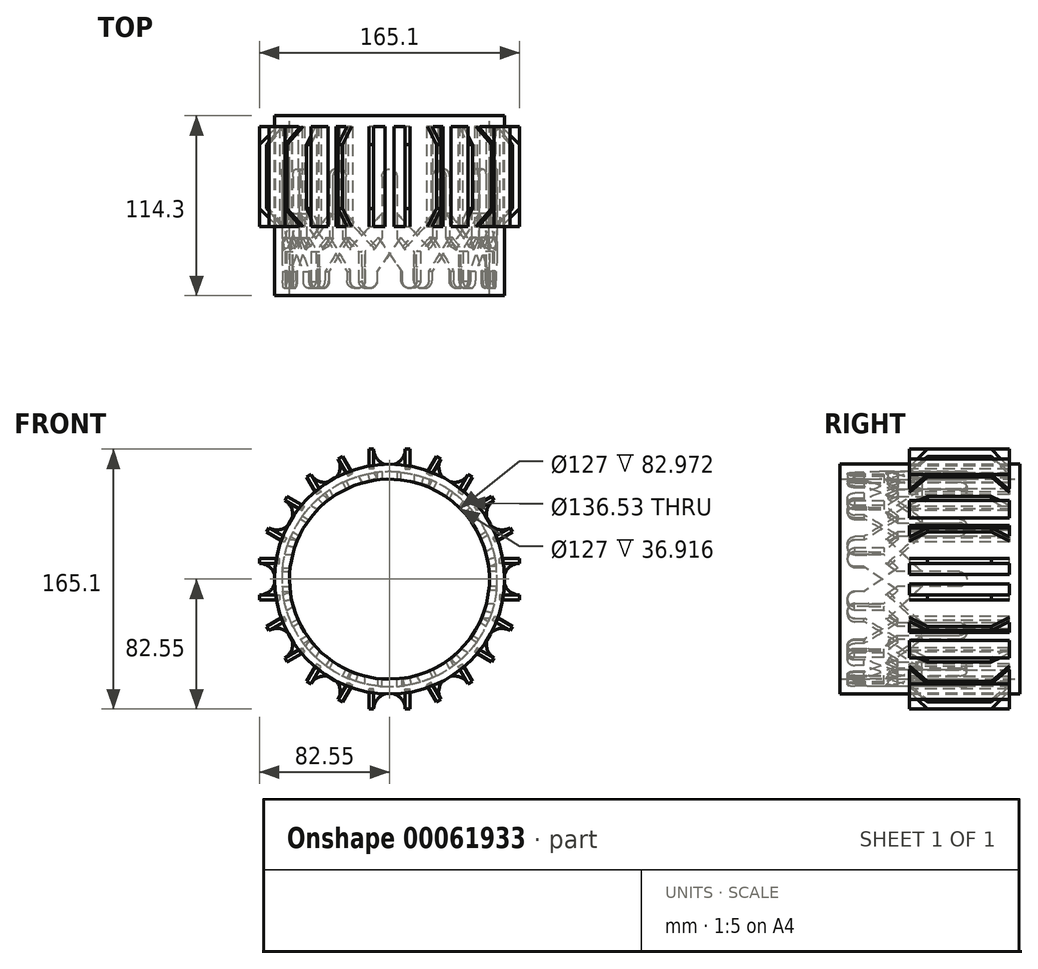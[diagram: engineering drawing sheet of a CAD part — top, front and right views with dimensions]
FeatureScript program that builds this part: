
annotation { "Feature Type Name" : "Feature", "Feature Type Description" : "" }
export const myFeature = defineFeature(function(context is Context, id is Id, definition is map)
    precondition{}
    {
        {
            var Q0;
            Q0=qCreatedBy(makeId("Front.planeOp"),FACE);
            var sketch = newSketch(context, id + "F0", { "sketchPlane" : qUnion([Q0])});
            skCircle(sketch, "E0", {"center": v(0, 0) * mm, "radius": 63.5 * mm});
            skCircle(sketch, "E1.0", {"center": v(0, 0) * mm, "radius": 73.03 * mm});
            skSolve(sketch);
        }
        {
            var Q0;
            Q0=makeQuery(id+"F0.imprint","IMPRINT",FACE,{"disambiguationData":[TD([[makeQuery(id+"F0.imprint","IMPRINT",EDGE,{"derivedFrom":sQuery(id+"F0.wireOp",EDGE,"E0")}),-1.0]])]});
            extrude(context, id + "F1", {"entities" : qUnion([Q0]), "depth" : 114.3 * mm});
        }
        {
            var Q0;
            Q0=qCreatedBy(makeId("Top.planeOp"),FACE);
            cPlane(context, id + "F2", {"entities" : qUnion([Q0]), "cplaneType" : CPlaneType.OFFSET, "offset" : 57.15 * mm, "width" : 152.4 * mm, "height" : 152.4 * mm});
        }
        {
            var Q0;
            Q0=qCreatedBy(id+"F2.planeOp",FACE);
            var sketch = newSketch(context, id + "F3", { "sketchPlane" : qUnion([Q0])});
            skLineSegment(sketch, "E2", {"start": v(0, -38.52) * mm, "end": v(0, -63.92) * mm});
            skCircle(sketch, "E3", {"center": v(20.32, -104.68) * mm, "radius": 4.76 * mm});
            skLineSegment(sketch, "E4.0", {"start": v(4.76, -62.17) * mm, "end": v(25.08, -83.88) * mm});
            skLineSegment(sketch, "E5", {"start": v(25.08, -83.88) * mm, "end": v(25.08, -104.8) * mm});
            skLineSegment(sketch, "E6", {"start": v(4.76, -62.17) * mm, "end": v(4.76, -38.52) * mm});
            skLineSegment(sketch, "E7", {"start": v(-4.76, -77.82) * mm, "end": v(-4.76, -38.52) * mm});
            skCircle(sketch, "E8", {"center": v(0, -38.52) * mm, "radius": 4.76 * mm});
            skLineSegment(sketch, "E9", {"start": v(4.76, -62.17) * mm, "end": v(4.76, -80.82) * mm});
            skLineSegment(sketch, "E10", {"start": v(7.16, -77.38) * mm, "end": v(-7.94, -99) * mm});
            skLineSegment(sketch, "E11", {"start": v(-7.94, -99) * mm, "end": v(-7.94, -104.68) * mm});
            skLineSegment(sketch, "E12.0", {"start": v(-17.46, -96) * mm, "end": v(-17.46, -104.68) * mm});
            skCircle(sketch, "E13", {"center": v(-12.7, -104.68) * mm, "radius": 4.76 * mm});
            skLineSegment(sketch, "E14.0", {"start": v(-4.76, -77.82) * mm, "end": v(-17.46, -96) * mm});
            skLineSegment(sketch, "E15.trimOffspring", {"start": v(7.16, -77.38) * mm, "end": v(15.59, -86.38) * mm});
            skPoint(sketch, "E16.orphan", {"position": v(-4.76, -65.66) * mm});
            skLineSegment(sketch, "E17.0", {"start": v(73.03, -114.3) * mm, "end": v(-73.03, -114.3) * mm});
            skLineSegment(sketch, "E18", {"start": v(15.59, -105.19) * mm, "end": v(15.59, -86.38) * mm});
            skSolve(sketch);
        }
        {
            var Q0;
            {var subQ7=sQuery(id+"F3.wireOp",EDGE,"E6");Q0=makeQuery(id+"F3.imprint","IMPRINT",FACE,{"disambiguationData":[TD([[makeQuery(id+"F3.imprint","IMPRINT",EDGE,{"derivedFrom":subQ7}),1.0]])]});}
            var Q1;
            {var subQ0=sQuery(id+"F3.wireOp",EDGE,"E13");var subQ1=makeQuery(id+"F3.imprint","INTERSECT",VERTEX,{"derivedFrom":[sQuery(id+"F3.wireOp",EDGE,"E11"),subQ0]});Q1=makeQuery(id+"F3.imprint","IMPRINT",FACE,{"disambiguationData":[TD([[makeQuery(id+"F3.imprint","IMPRINT",EDGE,{"disambiguationData":[TD([[subQ1,-1.0]])],"derivedFrom":subQ0}),1.0]])]});}
            var Q2;
            {var subQ0=sQuery(id+"F3.wireOp",EDGE,"E8");var subQ3=makeQuery(id+"F3.imprint","IMPRINT",VERTEX,{"derivedFrom":subQ0});Q2=makeQuery(id+"F3.imprint","IMPRINT",FACE,{"disambiguationData":[TD([[makeQuery(id+"F3.imprint","IMPRINT",EDGE,{"disambiguationData":[TD([[subQ3,1.0]])],"derivedFrom":subQ0}),1.0]])]});}
            var Q3;
            {var subQ1=sQuery(id+"F3.wireOp",EDGE,"E4.0");Q3=makeQuery(id+"F3.imprint","IMPRINT",FACE,{"disambiguationData":[TD([[makeQuery(id+"F3.imprint","IMPRINT",EDGE,{"derivedFrom":subQ1}),-1.0]])]});}
            var Q4;
            {var subQ0=sQuery(id+"F3.wireOp",EDGE,"E3");var subQ1=makeQuery(id+"F3.imprint","INTERSECT",VERTEX,{"derivedFrom":[subQ0,sQuery(id+"F3.wireOp",EDGE,"55f282a2-0efb-42c4-87fe-9c5e402fcb43.0")]});Q4=makeQuery(id+"F3.imprint","IMPRINT",FACE,{"disambiguationData":[TD([[makeQuery(id+"F3.imprint","IMPRINT",EDGE,{"disambiguationData":[TD([[subQ1,1.0]])],"derivedFrom":subQ0}),1.0]])]});}
            extrude(context, id + "F4", {"entities" : qUnion([Q0, Q1, Q2, Q3, Q4]), "depth" : 19.05 * mm});
        }
        {
            var Q0;
            Q0=makeQuery(id+"F4.opExtrude","SWEPT_BODY",BODY,{"disambiguationData":[OSD([sQuery(id+"F3.wireOp",EDGE,"E3"),sQuery(id+"F3.wireOp",EDGE,"E4.0"),sQuery(id+"F3.wireOp",EDGE,"E5"),sQuery(id+"F3.wireOp",EDGE,"E6"),sQuery(id+"F3.wireOp",EDGE,"E7"),sQuery(id+"F3.wireOp",EDGE,"E8"),sQuery(id+"F3.wireOp",EDGE,"55f282a2-0efb-42c4-87fe-9c5e402fcb43.0"),sQuery(id+"F3.wireOp",EDGE,"E10"),sQuery(id+"F3.wireOp",EDGE,"E11"),sQuery(id+"F3.wireOp",EDGE,"E12.0"),sQuery(id+"F3.wireOp",EDGE,"E13"),sQuery(id+"F3.wireOp",EDGE,"E14.0"),sQuery(id+"F3.wireOp",EDGE,"E15.trimOffspring")])]});
            var Q1;
            Q1=makeQuery(id+"F1.opExtrude","SWEPT_FACE",FACE,{"disambiguationData":[OSD([sQuery(id+"F0.wireOp",EDGE,"E0")])]});
            circularPattern(context, id + "F5", {"entities" : qUnion([Q0]), "axis" : qUnion([Q1]), "angle" : 30 * degree, "instanceCount" : 12});
        }
        {
            var Q0;
            Q0=makeQuery(id+"F5.opPattern","COPY",BODY,{"derivedFrom":makeQuery(id+"F4.opExtrude","SWEPT_BODY",BODY,{"disambiguationData":[OSD([sQuery(id+"F3.wireOp",EDGE,"E3"),sQuery(id+"F3.wireOp",EDGE,"E4.0"),sQuery(id+"F3.wireOp",EDGE,"E5"),sQuery(id+"F3.wireOp",EDGE,"E6"),sQuery(id+"F3.wireOp",EDGE,"E7"),sQuery(id+"F3.wireOp",EDGE,"E8"),sQuery(id+"F3.wireOp",EDGE,"55f282a2-0efb-42c4-87fe-9c5e402fcb43.0"),sQuery(id+"F3.wireOp",EDGE,"E10"),sQuery(id+"F3.wireOp",EDGE,"E11"),sQuery(id+"F3.wireOp",EDGE,"E12.0"),sQuery(id+"F3.wireOp",EDGE,"E13"),sQuery(id+"F3.wireOp",EDGE,"E14.0"),sQuery(id+"F3.wireOp",EDGE,"E15.trimOffspring")])]}),"instanceName":"1"});
            var Q1;
            Q1=makeQuery(id+"F4.opExtrude","SWEPT_BODY",BODY,{"disambiguationData":[OSD([sQuery(id+"F3.wireOp",EDGE,"E3"),sQuery(id+"F3.wireOp",EDGE,"E4.0"),sQuery(id+"F3.wireOp",EDGE,"E5"),sQuery(id+"F3.wireOp",EDGE,"E6"),sQuery(id+"F3.wireOp",EDGE,"E7"),sQuery(id+"F3.wireOp",EDGE,"E8"),sQuery(id+"F3.wireOp",EDGE,"55f282a2-0efb-42c4-87fe-9c5e402fcb43.0"),sQuery(id+"F3.wireOp",EDGE,"E10"),sQuery(id+"F3.wireOp",EDGE,"E11"),sQuery(id+"F3.wireOp",EDGE,"E12.0"),sQuery(id+"F3.wireOp",EDGE,"E13"),sQuery(id+"F3.wireOp",EDGE,"E14.0"),sQuery(id+"F3.wireOp",EDGE,"E15.trimOffspring")])]});
            var Q2;
            Q2=makeQuery(id+"F5.opPattern","COPY",BODY,{"derivedFrom":makeQuery(id+"F4.opExtrude","SWEPT_BODY",BODY,{"disambiguationData":[OSD([sQuery(id+"F3.wireOp",EDGE,"E3"),sQuery(id+"F3.wireOp",EDGE,"E4.0"),sQuery(id+"F3.wireOp",EDGE,"E5"),sQuery(id+"F3.wireOp",EDGE,"E6"),sQuery(id+"F3.wireOp",EDGE,"E7"),sQuery(id+"F3.wireOp",EDGE,"E8"),sQuery(id+"F3.wireOp",EDGE,"55f282a2-0efb-42c4-87fe-9c5e402fcb43.0"),sQuery(id+"F3.wireOp",EDGE,"E10"),sQuery(id+"F3.wireOp",EDGE,"E11"),sQuery(id+"F3.wireOp",EDGE,"E12.0"),sQuery(id+"F3.wireOp",EDGE,"E13"),sQuery(id+"F3.wireOp",EDGE,"E14.0"),sQuery(id+"F3.wireOp",EDGE,"E15.trimOffspring")])]}),"instanceName":"9"});
            var Q3;
            Q3=makeQuery(id+"F5.opPattern","COPY",BODY,{"derivedFrom":makeQuery(id+"F4.opExtrude","SWEPT_BODY",BODY,{"disambiguationData":[OSD([sQuery(id+"F3.wireOp",EDGE,"E3"),sQuery(id+"F3.wireOp",EDGE,"E4.0"),sQuery(id+"F3.wireOp",EDGE,"E5"),sQuery(id+"F3.wireOp",EDGE,"E6"),sQuery(id+"F3.wireOp",EDGE,"E7"),sQuery(id+"F3.wireOp",EDGE,"E8"),sQuery(id+"F3.wireOp",EDGE,"55f282a2-0efb-42c4-87fe-9c5e402fcb43.0"),sQuery(id+"F3.wireOp",EDGE,"E10"),sQuery(id+"F3.wireOp",EDGE,"E11"),sQuery(id+"F3.wireOp",EDGE,"E12.0"),sQuery(id+"F3.wireOp",EDGE,"E13"),sQuery(id+"F3.wireOp",EDGE,"E14.0"),sQuery(id+"F3.wireOp",EDGE,"E15.trimOffspring")])]}),"instanceName":"4"});
            var Q4;
            Q4=makeQuery(id+"F5.opPattern","COPY",BODY,{"derivedFrom":makeQuery(id+"F4.opExtrude","SWEPT_BODY",BODY,{"disambiguationData":[OSD([sQuery(id+"F3.wireOp",EDGE,"E3"),sQuery(id+"F3.wireOp",EDGE,"E4.0"),sQuery(id+"F3.wireOp",EDGE,"E5"),sQuery(id+"F3.wireOp",EDGE,"E6"),sQuery(id+"F3.wireOp",EDGE,"E7"),sQuery(id+"F3.wireOp",EDGE,"E8"),sQuery(id+"F3.wireOp",EDGE,"55f282a2-0efb-42c4-87fe-9c5e402fcb43.0"),sQuery(id+"F3.wireOp",EDGE,"E10"),sQuery(id+"F3.wireOp",EDGE,"E11"),sQuery(id+"F3.wireOp",EDGE,"E12.0"),sQuery(id+"F3.wireOp",EDGE,"E13"),sQuery(id+"F3.wireOp",EDGE,"E14.0"),sQuery(id+"F3.wireOp",EDGE,"E15.trimOffspring")])]}),"instanceName":"3"});
            var Q5;
            Q5=makeQuery(id+"F5.opPattern","COPY",BODY,{"derivedFrom":makeQuery(id+"F4.opExtrude","SWEPT_BODY",BODY,{"disambiguationData":[OSD([sQuery(id+"F3.wireOp",EDGE,"E3"),sQuery(id+"F3.wireOp",EDGE,"E4.0"),sQuery(id+"F3.wireOp",EDGE,"E5"),sQuery(id+"F3.wireOp",EDGE,"E6"),sQuery(id+"F3.wireOp",EDGE,"E7"),sQuery(id+"F3.wireOp",EDGE,"E8"),sQuery(id+"F3.wireOp",EDGE,"55f282a2-0efb-42c4-87fe-9c5e402fcb43.0"),sQuery(id+"F3.wireOp",EDGE,"E10"),sQuery(id+"F3.wireOp",EDGE,"E11"),sQuery(id+"F3.wireOp",EDGE,"E12.0"),sQuery(id+"F3.wireOp",EDGE,"E13"),sQuery(id+"F3.wireOp",EDGE,"E14.0"),sQuery(id+"F3.wireOp",EDGE,"E15.trimOffspring")])]}),"instanceName":"5"});
            var Q6;
            Q6=makeQuery(id+"F5.opPattern","COPY",BODY,{"derivedFrom":makeQuery(id+"F4.opExtrude","SWEPT_BODY",BODY,{"disambiguationData":[OSD([sQuery(id+"F3.wireOp",EDGE,"E3"),sQuery(id+"F3.wireOp",EDGE,"E4.0"),sQuery(id+"F3.wireOp",EDGE,"E5"),sQuery(id+"F3.wireOp",EDGE,"E6"),sQuery(id+"F3.wireOp",EDGE,"E7"),sQuery(id+"F3.wireOp",EDGE,"E8"),sQuery(id+"F3.wireOp",EDGE,"55f282a2-0efb-42c4-87fe-9c5e402fcb43.0"),sQuery(id+"F3.wireOp",EDGE,"E10"),sQuery(id+"F3.wireOp",EDGE,"E11"),sQuery(id+"F3.wireOp",EDGE,"E12.0"),sQuery(id+"F3.wireOp",EDGE,"E13"),sQuery(id+"F3.wireOp",EDGE,"E14.0"),sQuery(id+"F3.wireOp",EDGE,"E15.trimOffspring")])]}),"instanceName":"6"});
            var Q7;
            Q7=makeQuery(id+"F5.opPattern","COPY",BODY,{"derivedFrom":makeQuery(id+"F4.opExtrude","SWEPT_BODY",BODY,{"disambiguationData":[OSD([sQuery(id+"F3.wireOp",EDGE,"E3"),sQuery(id+"F3.wireOp",EDGE,"E4.0"),sQuery(id+"F3.wireOp",EDGE,"E5"),sQuery(id+"F3.wireOp",EDGE,"E6"),sQuery(id+"F3.wireOp",EDGE,"E7"),sQuery(id+"F3.wireOp",EDGE,"E8"),sQuery(id+"F3.wireOp",EDGE,"55f282a2-0efb-42c4-87fe-9c5e402fcb43.0"),sQuery(id+"F3.wireOp",EDGE,"E10"),sQuery(id+"F3.wireOp",EDGE,"E11"),sQuery(id+"F3.wireOp",EDGE,"E12.0"),sQuery(id+"F3.wireOp",EDGE,"E13"),sQuery(id+"F3.wireOp",EDGE,"E14.0"),sQuery(id+"F3.wireOp",EDGE,"E15.trimOffspring")])]}),"instanceName":"7"});
            var Q8;
            Q8=makeQuery(id+"F5.opPattern","COPY",BODY,{"derivedFrom":makeQuery(id+"F4.opExtrude","SWEPT_BODY",BODY,{"disambiguationData":[OSD([sQuery(id+"F3.wireOp",EDGE,"E3"),sQuery(id+"F3.wireOp",EDGE,"E4.0"),sQuery(id+"F3.wireOp",EDGE,"E5"),sQuery(id+"F3.wireOp",EDGE,"E6"),sQuery(id+"F3.wireOp",EDGE,"E7"),sQuery(id+"F3.wireOp",EDGE,"E8"),sQuery(id+"F3.wireOp",EDGE,"55f282a2-0efb-42c4-87fe-9c5e402fcb43.0"),sQuery(id+"F3.wireOp",EDGE,"E10"),sQuery(id+"F3.wireOp",EDGE,"E11"),sQuery(id+"F3.wireOp",EDGE,"E12.0"),sQuery(id+"F3.wireOp",EDGE,"E13"),sQuery(id+"F3.wireOp",EDGE,"E14.0"),sQuery(id+"F3.wireOp",EDGE,"E15.trimOffspring")])]}),"instanceName":"8"});
            var Q9;
            Q9=makeQuery(id+"F5.opPattern","COPY",BODY,{"derivedFrom":makeQuery(id+"F4.opExtrude","SWEPT_BODY",BODY,{"disambiguationData":[OSD([sQuery(id+"F3.wireOp",EDGE,"E3"),sQuery(id+"F3.wireOp",EDGE,"E4.0"),sQuery(id+"F3.wireOp",EDGE,"E5"),sQuery(id+"F3.wireOp",EDGE,"E6"),sQuery(id+"F3.wireOp",EDGE,"E7"),sQuery(id+"F3.wireOp",EDGE,"E8"),sQuery(id+"F3.wireOp",EDGE,"55f282a2-0efb-42c4-87fe-9c5e402fcb43.0"),sQuery(id+"F3.wireOp",EDGE,"E10"),sQuery(id+"F3.wireOp",EDGE,"E11"),sQuery(id+"F3.wireOp",EDGE,"E12.0"),sQuery(id+"F3.wireOp",EDGE,"E13"),sQuery(id+"F3.wireOp",EDGE,"E14.0"),sQuery(id+"F3.wireOp",EDGE,"E15.trimOffspring")])]}),"instanceName":"10"});
            var Q10;
            Q10=makeQuery(id+"F5.opPattern","COPY",BODY,{"derivedFrom":makeQuery(id+"F4.opExtrude","SWEPT_BODY",BODY,{"disambiguationData":[OSD([sQuery(id+"F3.wireOp",EDGE,"E3"),sQuery(id+"F3.wireOp",EDGE,"E4.0"),sQuery(id+"F3.wireOp",EDGE,"E5"),sQuery(id+"F3.wireOp",EDGE,"E6"),sQuery(id+"F3.wireOp",EDGE,"E7"),sQuery(id+"F3.wireOp",EDGE,"E8"),sQuery(id+"F3.wireOp",EDGE,"55f282a2-0efb-42c4-87fe-9c5e402fcb43.0"),sQuery(id+"F3.wireOp",EDGE,"E10"),sQuery(id+"F3.wireOp",EDGE,"E11"),sQuery(id+"F3.wireOp",EDGE,"E12.0"),sQuery(id+"F3.wireOp",EDGE,"E13"),sQuery(id+"F3.wireOp",EDGE,"E14.0"),sQuery(id+"F3.wireOp",EDGE,"E15.trimOffspring")])]}),"instanceName":"11"});
            var Q11;
            Q11=makeQuery(id+"F5.opPattern","COPY",BODY,{"derivedFrom":makeQuery(id+"F4.opExtrude","SWEPT_BODY",BODY,{"disambiguationData":[OSD([sQuery(id+"F3.wireOp",EDGE,"E3"),sQuery(id+"F3.wireOp",EDGE,"E4.0"),sQuery(id+"F3.wireOp",EDGE,"E5"),sQuery(id+"F3.wireOp",EDGE,"E6"),sQuery(id+"F3.wireOp",EDGE,"E7"),sQuery(id+"F3.wireOp",EDGE,"E8"),sQuery(id+"F3.wireOp",EDGE,"E10"),sQuery(id+"F3.wireOp",EDGE,"E11"),sQuery(id+"F3.wireOp",EDGE,"E12.0"),sQuery(id+"F3.wireOp",EDGE,"E13"),sQuery(id+"F3.wireOp",EDGE,"E14.0"),sQuery(id+"F3.wireOp",EDGE,"E15.trimOffspring"),sQuery(id+"F3.wireOp",EDGE,"E18")])]}),"instanceName":"2"});
            var Q12;
            Q12=makeQuery(id+"F1.opExtrude","SWEPT_BODY",BODY,{"disambiguationData":[OSD([sQuery(id+"F0.wireOp",EDGE,"E0"),sQuery(id+"F0.wireOp",EDGE,"E1.0")])]});
            booleanBodies(context, id + "F6", {"operationType" : BooleanOperationType.SUBTRACTION, "tools" : qUnion([Q0, Q1, Q2, Q3, Q4, Q5, Q6, Q7, Q8, Q9, Q10, Q11]), "targets" : qUnion([Q12])});
        }
        {
            var Q0;
            Q0=makeQuery(id+"F1.opExtrude","CAP_FACE",FACE,{"disambiguationData":[OSD([sQuery(id+"F0.wireOp",EDGE,"E0"),sQuery(id+"F0.wireOp",EDGE,"E1.0")])],"isStart":false});
            var sketch = newSketch(context, id + "F7", { "sketchPlane" : qUnion([Q0])});
            skCircle(sketch, "E19.0", {"center": v(0, 0) * mm, "radius": 73.03 * mm});
            skCircle(sketch, "E20.0", {"center": v(0, 0) * mm, "radius": 68.26 * mm});
            skSolve(sketch);
        }
        {
            var Q0;
            Q0=makeQuery(id+"F7.imprint","IMPRINT",FACE,{"disambiguationData":[TD([[makeQuery(id+"F7.imprint","IMPRINT",EDGE,{"derivedFrom":sQuery(id+"F7.wireOp",EDGE,"E19.0")}),1.0]])]});
            var Q1;
            Q1=makeQuery(id+"F1.opExtrude","CAP_FACE",FACE,{"disambiguationData":[OSD([sQuery(id+"F0.wireOp",EDGE,"E0"),sQuery(id+"F0.wireOp",EDGE,"E1.0")])],"isStart":true});
            extrude(context, id + "F8", {"entities" : qUnion([Q0]), "endBound" : BoundingType.UP_TO_SURFACE, "oppositeDirection" : true, "endBoundEntityFace" : qUnion([Q1]), "depth" : 25.4 * mm});
        }
        {
            var Q0;
            Q0=makeQuery(id+"F6.opBoolean","SPLIT",BODY,{"disambiguationData":[OD(0.0)],"derivedFrom":makeQuery(id+"F1.opExtrude","SWEPT_BODY",BODY,{"disambiguationData":[OSD([sQuery(id+"F0.wireOp",EDGE,"E0"),sQuery(id+"F0.wireOp",EDGE,"E1.0")])]})});
            var Q1;
            Q1=makeQuery(id+"F6.opBoolean","SPLIT",BODY,{"disambiguationData":[OD(1.0)],"derivedFrom":makeQuery(id+"F1.opExtrude","SWEPT_BODY",BODY,{"disambiguationData":[OSD([sQuery(id+"F0.wireOp",EDGE,"E0"),sQuery(id+"F0.wireOp",EDGE,"E1.0")])]})});
            var Q2;
            Q2=makeQuery(id+"F8.opExtrude","SWEPT_BODY",BODY,{"disambiguationData":[OSD([sQuery(id+"F7.wireOp",EDGE,"E19.0"),sQuery(id+"F7.wireOp",EDGE,"E20.0")])]});
            booleanBodies(context, id + "F9", {"operationType" : BooleanOperationType.UNION, "tools" : qUnion([Q0, Q1, Q2])});
        }
        {
            var Q0;
            Q0=qCreatedBy(id+"F2.planeOp",FACE);
            cPlane(context, id + "F10", {"entities" : qUnion([Q0]), "cplaneType" : CPlaneType.OFFSET, "offset" : 12.7 * mm, "width" : 152.4 * mm, "height" : 152.4 * mm});
        }
        {
            var Q0;
            Q0=qCreatedBy(id+"F10.planeOp",FACE);
            var sketch = newSketch(context, id + "F11", { "sketchPlane" : qUnion([Q0])});
            skLineSegment(sketch, "E21.0", {"start": v(-4.76, -77.82) * mm, "end": v(-4.76, -38.52) * mm});
            skLineSegment(sketch, "E22.0", {"start": v(4.76, -62.17) * mm, "end": v(4.76, -38.52) * mm});
            skLineSegment(sketch, "E23", {"start": v(-4.76, -38.52) * mm, "end": v(4.76, -38.52) * mm});
            skLineSegment(sketch, "E24.rect.left", {"start": v(-10, -6.77) * mm, "end": v(-10, -70.27) * mm});
            skLineSegment(sketch, "E24.rect.right", {"start": v(10, -6.77) * mm, "end": v(10, -70.27) * mm});
            skPoint(sketch, "E24.rect.middle", {"position": v(0, -38.52) * mm});
            skLineSegment(sketch, "E25", {"start": v(-13.13, -6.77) * mm, "end": v(-13.13, -70.27) * mm});
            skLineSegment(sketch, "E26", {"start": v(-10, -6.77) * mm, "end": v(-13.13, -6.77) * mm});
            skLineSegment(sketch, "E27", {"start": v(-13.13, -70.27) * mm, "end": v(-10, -70.27) * mm});
            skSolve(sketch);
        }
        {
            var Q0;
            Q0 = qSketchRegion(id + "F11", true);
            extrude(context, id + "F12", {"entities" : qUnion([Q0]), "depth" : 12.7 * mm});
        }
        {
            var Q0;
            Q0=makeQuery(id+"F12.opExtrude","SWEPT_BODY",BODY,{"disambiguationData":[OSD([sQuery(id+"F11.wireOp",EDGE,"E24.rect.left"),sQuery(id+"F11.wireOp",EDGE,"E25"),sQuery(id+"F11.wireOp",EDGE,"E27"),sQuery(id+"F11.wireOp",EDGE,"E26")])]});
            var Q1;
            Q1=qCreatedBy(makeId("Right.planeOp"),FACE);
            mirror(context, id + "F13", {"entities" : qUnion([Q0]), "mirrorPlane" : qUnion([Q1])});
        }
        {
            var Q0;
            Q0=makeQuery(id+"F13.opPattern","COPY",FACE,{"derivedFrom":makeQuery(id+"F12.opExtrude","SWEPT_FACE",FACE,{"disambiguationData":[OSD([sQuery(id+"F11.wireOp",EDGE,"E26")])]}),"instanceName":"1"});
            var sketch = newSketch(context, id + "F14", { "sketchPlane" : qUnion([Q0])});
            skCircle(sketch, "E28.0", {"center": v(0, 0) * mm, "radius": 73.03 * mm});
            skLineSegment(sketch, "E29.0", {"start": v(10, 82.55) * mm, "end": v(13.13, 82.55) * mm});
            skLineSegment(sketch, "E30.0", {"start": v(-10, 82.55) * mm, "end": v(-13.13, 82.55) * mm});
            skLineSegment(sketch, "E31", {"start": v(10, 82.55) * mm, "end": v(10, 72.34) * mm});
            skPoint(sketch, "E32.endSnap0", {"position": v(-10, 76.2) * mm});
            skPoint(sketch, "E32.endSnap1", {"position": v(10, 77.44) * mm});
            skLineSegment(sketch, "E33", {"start": v(10, 82.55) * mm, "end": v(-10, 82.55) * mm});
            skArc(sketch, "E34", {"start": v(-10, 82.55) * mm, "mid": v(-8.03, 76.58) * mm, "end": v(-2.89, 72.97) * mm});
            skArc(sketch, "E35", {"start": v(10, 82.55) * mm, "mid": v(8.03, 76.58) * mm, "end": v(2.89, 72.97) * mm});
            skPoint(sketch, "E36.orphan", {"position": v(0, 72.54) * mm});
            skSolve(sketch);
        }
        {
            var Q0;
            {var subQ0=sQuery(id+"F14.wireOp",EDGE,"E34");Q0=makeQuery(id+"F14.imprint","IMPRINT",FACE,{"disambiguationData":[TD([[makeQuery(id+"F14.imprint","IMPRINT",EDGE,{"derivedFrom":subQ0}),-1.0]])]});}
            var Q1;
            {var subQ0=sQuery(id+"F14.wireOp",EDGE,"E31");Q1=makeQuery(id+"F14.imprint","IMPRINT",FACE,{"disambiguationData":[TD([[makeQuery(id+"F14.imprint","IMPRINT",EDGE,{"derivedFrom":subQ0}),-1.0]])]});}
            var Q2;
            Q2=makeQuery(id+"F13.opPattern","COPY",FACE,{"derivedFrom":makeQuery(id+"F12.opExtrude","SWEPT_FACE",FACE,{"disambiguationData":[OSD([sQuery(id+"F11.wireOp",EDGE,"E27")])]}),"instanceName":"1"});
            extrude(context, id + "F15", {"entities" : qUnion([Q0, Q1]), "endBound" : BoundingType.UP_TO_SURFACE, "oppositeDirection" : true, "endBoundEntityFace" : qUnion([Q2]), "depth" : 25.4 * mm});
        }
        {
            var Q0;
            Q0=makeQuery(id+"F13.opPattern","COPY",EDGE,{"derivedFrom":makeQuery(id+"F12.opExtrude","CAP_EDGE",EDGE,{"disambiguationData":[OSD([sQuery(id+"F11.wireOp",EDGE,"E26")])],"isStart":false}),"instanceName":"1"});
            var Q1;
            Q1=makeQuery(id+"F12.opExtrude","CAP_EDGE",EDGE,{"disambiguationData":[OSD([sQuery(id+"F11.wireOp",EDGE,"E26")])],"isStart":false});
            var Q2;
            Q2=makeQuery(id+"F12.opExtrude","CAP_EDGE",EDGE,{"disambiguationData":[OSD([sQuery(id+"F11.wireOp",EDGE,"E27")])],"isStart":false});
            var Q3;
            Q3=makeQuery(id+"F13.opPattern","COPY",EDGE,{"derivedFrom":makeQuery(id+"F12.opExtrude","CAP_EDGE",EDGE,{"disambiguationData":[OSD([sQuery(id+"F11.wireOp",EDGE,"E27")])],"isStart":false}),"instanceName":"1"});
            chamfer(context, id + "F16", {"entities" : qUnion([Q0, Q1, Q2, Q3]), "width" : 11.43 * mm, "tangentPropagation" : true});
        }
        {
            var Q0;
            Q0=makeQuery(id+"F13.opPattern","COPY",BODY,{"derivedFrom":makeQuery(id+"F12.opExtrude","SWEPT_BODY",BODY,{"disambiguationData":[OSD([sQuery(id+"F11.wireOp",EDGE,"E24.rect.left"),sQuery(id+"F11.wireOp",EDGE,"E25"),sQuery(id+"F11.wireOp",EDGE,"E27"),sQuery(id+"F11.wireOp",EDGE,"E26")])]}),"instanceName":"1"});
            var Q1;
            Q1=makeQuery(id+"F12.opExtrude","SWEPT_BODY",BODY,{"disambiguationData":[OSD([sQuery(id+"F11.wireOp",EDGE,"E24.rect.left"),sQuery(id+"F11.wireOp",EDGE,"E25"),sQuery(id+"F11.wireOp",EDGE,"E27"),sQuery(id+"F11.wireOp",EDGE,"E26")])]});
            var Q2;
            Q2=makeQuery(id+"F15.opExtrude","SWEPT_BODY",BODY,{"disambiguationData":[OSD([sQuery(id+"F14.wireOp",EDGE,"E28.0"),sQuery(id+"F14.wireOp",EDGE,"E31"),sQuery(id+"F14.wireOp",EDGE,"E35")])]});
            var Q3;
            Q3=makeQuery(id+"F15.opExtrude","SWEPT_BODY",BODY,{"disambiguationData":[OSD([sQuery(id+"F11.wireOp",EDGE,"E24.rect.left"),sQuery(id+"F11.wireOp",EDGE,"E26"),sQuery(id+"F14.wireOp",EDGE,"E28.0"),sQuery(id+"F14.wireOp",EDGE,"E34")])]});
            var Q4;
            {var subQ0=makeQuery(id+"F4.opExtrude","SWEPT_FACE",FACE,{"disambiguationData":[OSD([sQuery(id+"F3.wireOp",EDGE,"E3")])]});var subQ6=sQuery(id+"F0.wireOp",EDGE,"E1.0");var subQ8=makeQuery(id+"F1.opExtrude","SWEPT_FACE",FACE,{"disambiguationData":[OSD([subQ6])]});var subQ9=makeQuery(id+"F4.opExtrude","SWEPT_FACE",FACE,{"disambiguationData":[OSD([sQuery(id+"F3.wireOp",EDGE,"E4.0")])]});Q4=makeQuery(id+"F9.opBoolean","MERGE",FACE,{"derivedFrom":[makeQuery(id+"F6.opBoolean","SPLIT",FACE,{"disambiguationData":[TD([subQ9])],"derivedFrom":subQ8}),makeQuery(id+"F6.opBoolean","SPLIT",FACE,{"disambiguationData":[TD([subQ0])],"derivedFrom":subQ8}),makeQuery(id+"F8.opExtrude","SWEPT_FACE",FACE,{"disambiguationData":[OSD([sQuery(id+"F7.wireOp",EDGE,"E19.0")])]})]});}
            circularPattern(context, id + "F17", {"entities" : qUnion([Q0, Q1, Q2, Q3]), "axis" : qUnion([Q4]), "angle" : 30 * degree, "instanceCount" : 12});
        }
    });
